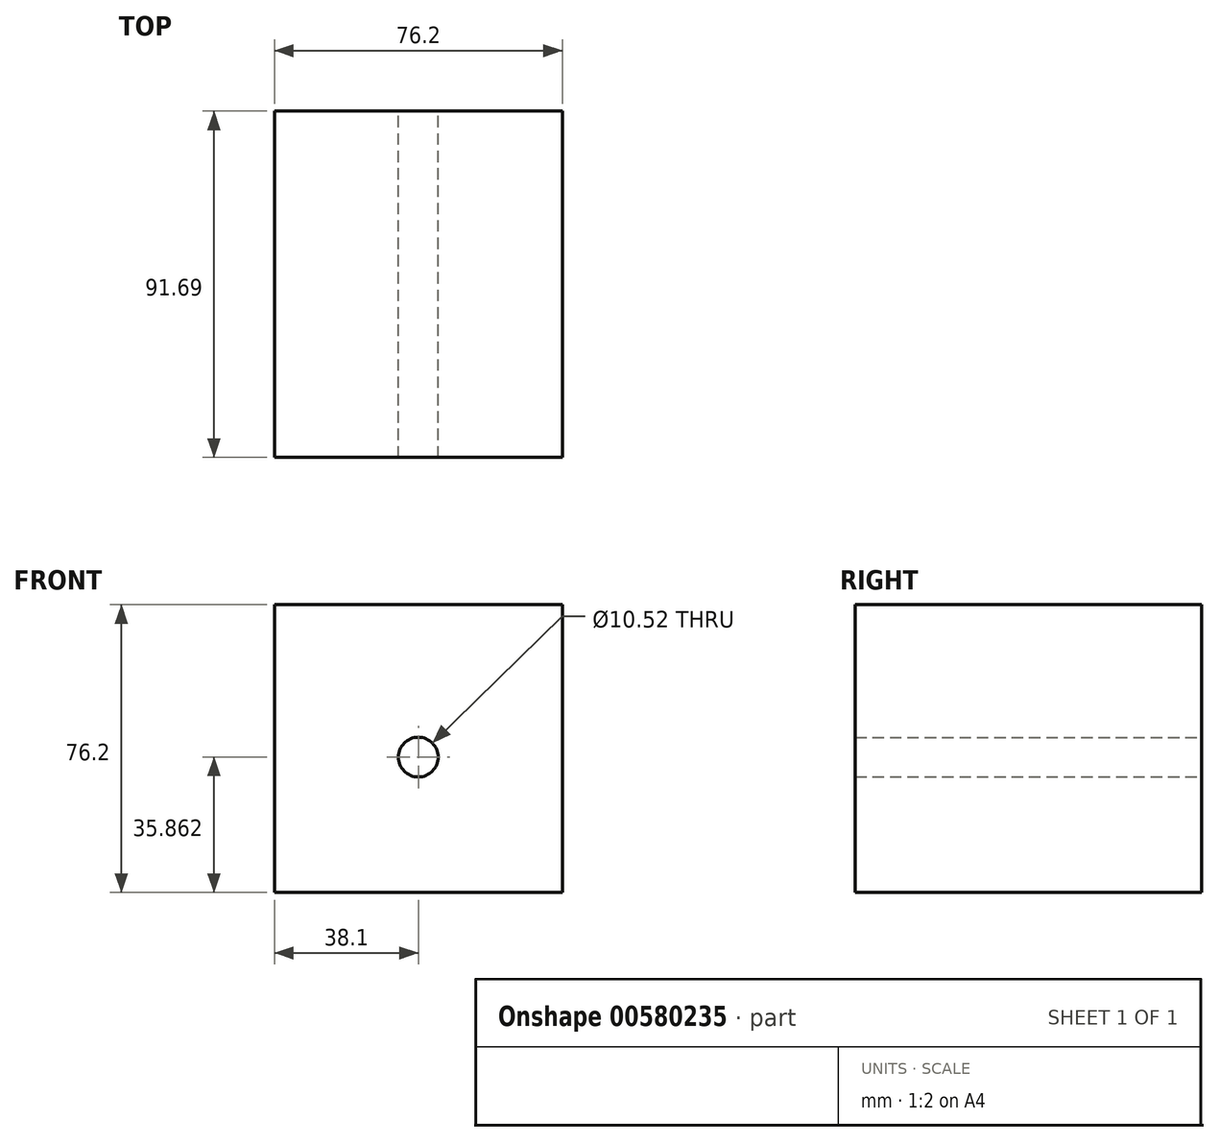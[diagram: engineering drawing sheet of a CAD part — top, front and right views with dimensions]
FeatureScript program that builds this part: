
annotation { "Feature Type Name" : "Feature", "Feature Type Description" : "" }
export const myFeature = defineFeature(function(context is Context, id is Id, definition is map)
    precondition{}
    {
        {
            var Q0;
            Q0=qCreatedBy(makeId("Front.planeOp"),FACE);
            var sketch = newSketch(context, id + "F0", { "sketchPlane" : qUnion([Q0])});
            skLineSegment(sketch, "E0.bottom", {"start": v(0, 0) * mm, "end": v(76.2, 0) * mm});
            skLineSegment(sketch, "E0.top", {"start": v(0, 76.2) * mm, "end": v(76.2, 76.2) * mm});
            skLineSegment(sketch, "E0.left", {"start": v(0, 0) * mm, "end": v(0, 76.2) * mm});
            skLineSegment(sketch, "E0.right", {"start": v(76.2, 0) * mm, "end": v(76.2, 76.2) * mm});
            skCircle(sketch, "E1", {"center": v(38.1, 35.86) * mm, "radius": 5.26 * mm});
            skSolve(sketch);
        }
        {
            var Q0;
            Q0=makeQuery(id+"F0.imprint","IMPRINT",FACE,{"disambiguationData":[TD([[makeQuery(id+"F0.imprint","IMPRINT",EDGE,{"derivedFrom":sQuery(id+"F0.wireOp",EDGE,"E0.bottom")}),1.0]])]});
            extrude(context, id + "F1", {"entities" : qUnion([Q0]), "depth" : 91.7 * mm, "offsetDistance" : 25.4 * mm});
        }
        {
            var Q0;
            Q0 = qSketchRegion(id + "F0", true);
            extrude(context, id + "F2", {"entities" : qUnion([Q0]), "operationType" : NewBodyOperationType.ADD, "depth" : 25.4 * mm, "offsetDistance" : 25.4 * mm});
        }
    });
